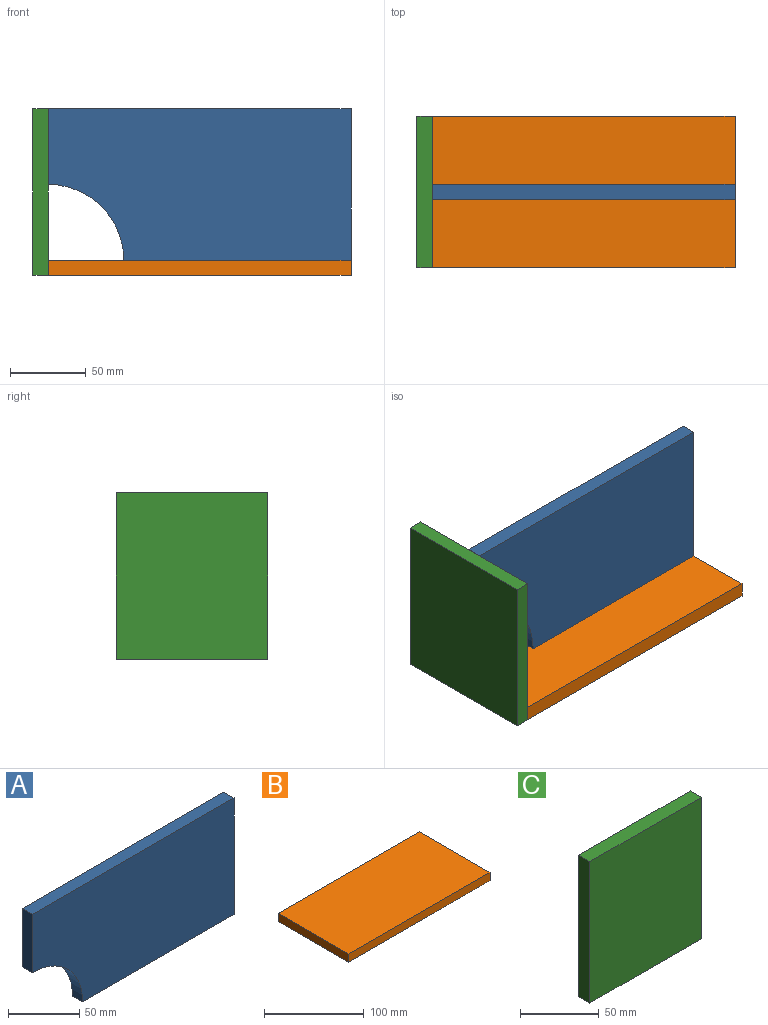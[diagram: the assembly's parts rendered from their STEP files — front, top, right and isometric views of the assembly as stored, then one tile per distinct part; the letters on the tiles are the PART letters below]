
ASSEMBLY  parts=3 mates=6
PART A: 7 faces, bbox 200x10x100 mm
  f0: plane 100x10mm, normal (1,0,0), area 1000mm2, adj f1,f4,f5,f6
  f1: plane 200x10mm, normal (0,0,1), area 2000mm2, adj f0,f2,f5,f6
  f2: plane 50x10mm, normal (-1,0,0), area 500mm2, adj f1,f3,f5,f6
  f3: cylinder r=50mm len=50mm, axis (0,1,0), area 785.4mm2, adj f2,f4,f5,f6
  f4: plane 150x10mm, normal (0,0,-1), area 1500mm2, adj f0,f3,f5,f6
  f5: plane 200x100mm, normal (0,-1,0), area 18036.5mm2, adj f0,f1,f2,f3,f4
  f6: plane 200x100mm, normal (0,1,0), area 18036.5mm2, adj f0,f1,f2,f3,f4
PART B: 6 faces, bbox 200x100x10 mm
  f0: plane 200x10mm, normal (0,1,0), area 2000mm2, adj f1,f3,f4,f5
  f1: plane 100x10mm, normal (-1,0,0), area 1000mm2, adj f0,f2,f4,f5
  f2: plane 200x10mm, normal (0,-1,0), area 2000mm2, adj f1,f3,f4,f5
  f3: plane 100x10mm, normal (1,0,0), area 1000mm2, adj f0,f2,f4,f5
  f4: plane 200x100mm, normal (0,0,1), area 20000mm2, adj f0,f1,f2,f3
  f5: plane 200x100mm, normal (0,0,-1), area 20000mm2, adj f0,f1,f2,f3
PART C: 6 faces, bbox 100x10x110 mm
  f0: plane 100x10mm, normal (0,0,1), area 1000mm2, adj f1,f3,f4,f5
  f1: plane 110x10mm, normal (-1,0,0), area 1100mm2, adj f0,f2,f4,f5
  f2: plane 100x10mm, normal (0,0,-1), area 1000mm2, adj f1,f3,f4,f5
  f3: plane 110x10mm, normal (1,0,0), area 1100mm2, adj f0,f2,f4,f5
  f4: plane 110x100mm, normal (0,-1,0), area 11000mm2, adj f0,f1,f2,f3
  f5: plane 110x100mm, normal (0,1,0), area 11000mm2, adj f0,f1,f2,f3
PLACE A t=(208.74,-38.13,74)mm
PLACE B t=(208.74,-38.13,14)mm
PLACE C rot(axis=(0,0,1),90deg) t=(103.74,-38.13,69)mm
MATE parallel C.f2 <-> B.f5  axis (0,0,-1) through (98.74,-38.13,14)mm
MATE planar C.f4 <-> B.f1  axis (1,0,0) through (108.74,-38.13,14)mm
MATE planar A.f4 <-> B.f4  axis (0,0,-1) through (233.74,-38.13,24)mm
MATE parallel A.f0 <-> B.f3  axis (1,0,0) through (308.74,-38.13,74)mm
MATE parallel A.f5 <-> B.f2  axis (0,-1,0) through (217.32,-43.13,77.14)mm
MATE parallel C.f1 <-> B.f2  axis (0,-1,0) through (103.74,-88.13,69)mm
